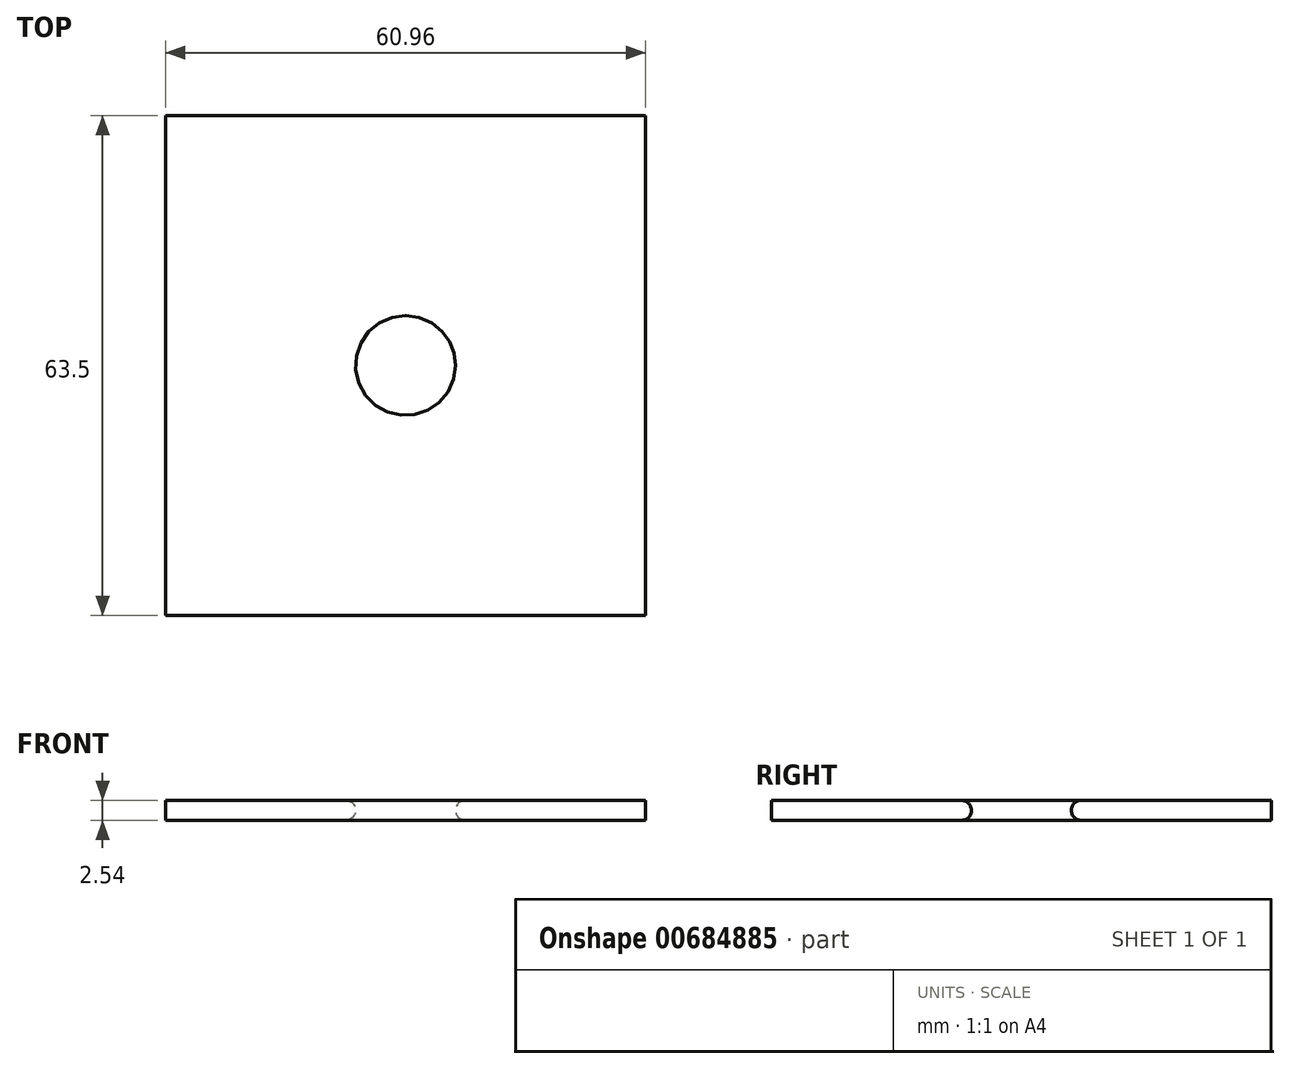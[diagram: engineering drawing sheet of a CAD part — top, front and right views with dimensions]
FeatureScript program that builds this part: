
annotation { "Feature Type Name" : "Feature", "Feature Type Description" : "" }
export const myFeature = defineFeature(function(context is Context, id is Id, definition is map)
    precondition{}
    {
        {
            var Q0;
            Q0=qCreatedBy(makeId("Top.planeOp"),FACE);
            var sketch = newSketch(context, id + "F0", { "sketchPlane" : qUnion([Q0])});
            skLineSegment(sketch, "E0.bottom", {"start": v(-30.48, 31.75) * mm, "end": v(30.48, 31.75) * mm});
            skLineSegment(sketch, "E0.top", {"start": v(-30.48, -31.75) * mm, "end": v(30.48, -31.75) * mm});
            skLineSegment(sketch, "E0.left", {"start": v(-30.48, 31.75) * mm, "end": v(-30.48, -31.75) * mm});
            skLineSegment(sketch, "E0.right", {"start": v(30.48, 31.75) * mm, "end": v(30.48, -31.75) * mm});
            skPoint(sketch, "E0.middle", {"position": v(0, 0) * mm});
            skCircle(sketch, "E1", {"center": v(0, 0) * mm, "radius": 6.35 * mm});
            skSolve(sketch);
        }
        {
            var Q0;
            Q0=makeQuery(id+"F0.imprint","IMPRINT",FACE,{"disambiguationData":[TD([[makeQuery(id+"F0.imprint","IMPRINT",EDGE,{"derivedFrom":sQuery(id+"F0.wireOp",EDGE,"E0.bottom")}),-1.0]])]});
            extrude(context, id + "F1", {"entities" : qUnion([Q0]), "depth" : 2.54 * mm, "offsetDistance" : 25.4 * mm});
        }
        {
            var Q0;
            Q0=makeQuery(id+"F1.opExtrude","CAP_EDGE",EDGE,{"disambiguationData":[OSD([sQuery(id+"F0.wireOp",EDGE,"E1")])],"isStart":false});
            var Q1;
            Q1=makeQuery(id+"F1.opExtrude","CAP_EDGE",EDGE,{"disambiguationData":[OSD([sQuery(id+"F0.wireOp",EDGE,"E1")])],"isStart":true});
            fillet(context, id + "F2", {"entities" : qUnion([Q0, Q1]), "radius" : 1.27 * mm, "tangentPropagation" : true, "allowEdgeOverflow" : false});
        }
    });
